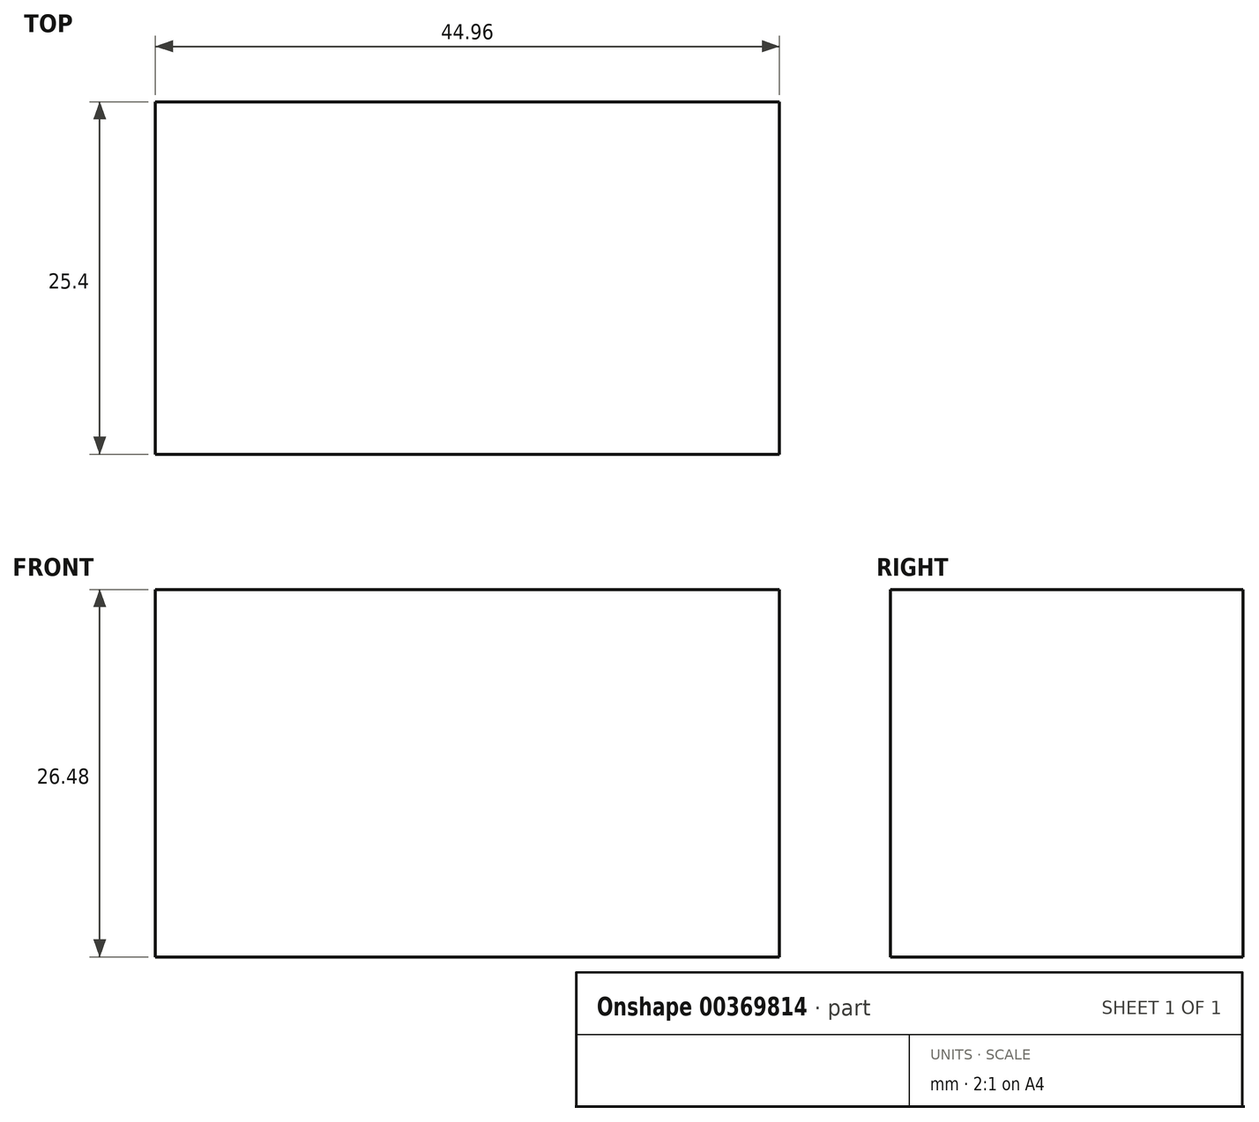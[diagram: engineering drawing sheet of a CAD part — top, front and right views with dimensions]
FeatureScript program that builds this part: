
annotation { "Feature Type Name" : "Feature", "Feature Type Description" : "" }
export const myFeature = defineFeature(function(context is Context, id is Id, definition is map)
    precondition{}
    {
        {
            var Q0;
            Q0=qCreatedBy(makeId("Front.planeOp"),FACE);
            var sketch = newSketch(context, id + "F0", { "sketchPlane" : qUnion([Q0])});
            skLineSegment(sketch, "E0.bottom", {"start": v(0, 0) * mm, "end": v(44.96, 0) * mm});
            skLineSegment(sketch, "E0.top", {"start": v(0, -26.48) * mm, "end": v(44.96, -26.48) * mm});
            skLineSegment(sketch, "E0.left", {"start": v(0, 0) * mm, "end": v(0, -26.48) * mm});
            skLineSegment(sketch, "E0.right", {"start": v(44.96, 0) * mm, "end": v(44.96, -26.48) * mm});
            skSolve(sketch);
        }
        {
            var Q0;
            Q0=makeQuery(id+"F0.imprint","IMPRINT",FACE,{"disambiguationData":[TD([[makeQuery(id+"F0.imprint","IMPRINT",EDGE,{"derivedFrom":sQuery(id+"F0.wireOp",EDGE,"E0.bottom")}),-1.0]])]});
            extrude(context, id + "F1", {"entities" : qUnion([Q0]), "depth" : 25.4 * mm});
        }
    });
